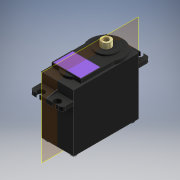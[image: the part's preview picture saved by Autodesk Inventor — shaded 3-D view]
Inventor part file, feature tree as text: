
AUTODESK INVENTOR PART (.ipt)
format: ipt  version: 2019 (Build 230136000, 136)  size: 515,584 bytes
history: native  units: mm
features: sketch x17, extrude x15, projected_geometry x6, mirror x5, plane x3, fillet x3, chamfer x1, loft x1
ambient origin geometry x8: Origin, YZ Plane, XZ Plane, XY Plane, X Axis, Y Axis, Z Axis, Center Point
bodies: Solid1 (feature_tree)
feature tree (51):
  extrude  "Extrusion1"  Depth=40.0mm
  chamfer  "Chamfer1"  Distance=36.88mm
  plane  "Work Plane1"
  extrude  "Extrusion2"  [1 undecoded]
  mirror  "Mirror1"
  mirror  "Mirror2"
  extrude  "Extrusion4"  Depth=36.88mm TaperAngle=0.0deg
  fillet  "Fillet1"  Radius=3.2mm
  extrude  "Extrusion5"  Depth=0.3mm
  fillet  "Fillet2"  Radius=0.7mm
  mirror  "Mirror3"
  mirror  "Mirror4"
  extrude  "Extrusion6"  Depth=2.2mm
  plane  "Work Plane3"
  loft  "Loft1"
  extrude  "Extrusion7"  Depth=3.9mm
  extrude  "Extrusion8"  Depth=4.0mm
  extrude  "Extrusion9"  TaperAngle=0.0deg  [1 undecoded]
  extrude  "Extrusion10"  TaperAngle=90.0deg  [1 undecoded]
  fillet  "Fillet3"  Radius=2.4mm
  extrude  "Extrusion11"  Depth=0.2mm TaperAngle=0.0deg
  extrude  "Extrusion12"  Depth=1.7mm TaperAngle=0.0deg
  extrude  "Extrusion13"  Depth=13.0mm
  extrude  "Extrusion15"  Depth=10.0mm
  plane  "Work Plane4"
  extrude  "Extrusion16"  Depth=6.0mm
  extrude  "Extrusion17"  Depth=3.0mm
  mirror  "Mirror5"
  sketch  "Sketch1"  dims[d0=20.0mm d1=40.0mm d2=36.88mm d3=0.0mm]
  sketch  "Sketch2"  dims[d4=1.64mm d5=2.0mm d6=45.0deg d7=-1.0mm]
  sketch  "Sketch3"  dims[d8=8.0mm d9=36.88mm d10=0.0mm d16=3.2mm]
  sketch  "Sketch4"  dims[d17=0.8mm d18=0.0mm d20=0.3mm d21=0.7mm]
  sketch  "Sketch5"  dims[d22=2.2mm d23=0.7mm d24=2.2mm]
  sketch  "Sketch6"  dims[d25=0.5mm d26=0.0mm d27=0.05mm]
  sketch  "Sketch7"  dims[d30=6.6mm d31=3.9mm]
  sketch  "Sketch8"  dims[d32=0.8mm d33=0.0mm d34=4.0mm]
  sketch  "Sketch9"  dims[d35=0.0mm d36=90.0deg d37=0.0mm d38=90.0deg]
  sketch  "Sketch10"  dims[d39=9.0mm d40=90.0deg d44=2.4mm d45=0.0mm]
  sketch  "Sketch11"  dims[d46=12.76mm d47=0.2mm d48=0.0mm]
  sketch  "Sketch12"  dims[d49=0.1mm d50=0.0mm d53=1.7mm d54=0.0mm]
  sketch  "Sketch13"  dims[d55=0.1mm d56=13.0mm]
  sketch  "Sketch14"  dims[d57=1.2mm d58=0.0mm d59=10.0mm]
  sketch  "Sketch17"  dims[d60=0.2mm d61=0.0mm d62=6.0mm]
  sketch  "Sketch18"  dims[d63=3.2mm d64=0.0mm d69=3.0mm]
  sketch  "Sketch19"  dims[d70=3.0mm d71=0.0mm d72=-8.4mm d73=7.0mm d74=2.0mm d77=19.8mm d78=4.4mm d79=2.4mm d80=0.0mm d81=1.4mm d82=0.5mm d83=0.0mm]
  projected_geometry  "Project Cut Edges1"
  projected_geometry  "Project Cut Edges2"
  projected_geometry  "Project Cut Edges3"
  projected_geometry  "Project Cut Edges5"
  projected_geometry  "Project Cut Edges6"
  projected_geometry  "Project Cut Edges8"
note: 3 required parameter values undecoded (feature->parameter linkage not recoverable at this tier; creation-order binding heuristic only, values carry confidence <= 0.55)
